# Revit family: PlumFix_Tap_ABEY_Stile_Wall Mixer & Basin Spout Set
name_source: partatom
category: Plumbing Fixtures
revit_build: Autodesk Revit 2015 (Build: 20140223_1515(x64)
units: mm (PartAtom-declared; Revit-internal decimal feet)

## types (5) — shared parameters
CW Connection = Yes
Description = Stile Wall Mixer & Basin Spout Set
HW Connection = Yes
Manufacturer = Abey Australia
Manufacturer_Overall Depth = 201 mm
Manufacturer_Overall Height = 110 mm
Manufacturer_Overall Width = 250 mm  [stored 0.82021 ft]
Manufacturer_URL__Product Specific = https://www.abey.com.au
URL = https://www.abey.com.au
Vent Connection = No
Waste Connection = No
zero-valued in all types: CWFU, Cost, HWFU, WFU

## per-type parameters (varying)
| type | Manufacturer_Spec Code | Model | PlumbingMaterial_ANZRS | Type Comments |
| Chrome | 700197+300033 | 700197+300033 | z_Abey_Chrome | Chrome Finish |
| Black | 700197B+300033B | 700197B+300033B | z_Abey_Black | Black Finish |
| Brushed Nickel | 700197BN+300033BN | 700197BN+300033BN | z_Abey_Brushed Nickel | Brushed Nickel Finish |
| Graphite | 700197GR+300033GR | 700197GR+300033GR | z_Abey_Graphite | Graphite Finish |
| Rose Gold | 700197RG+300033RG | 700197RG+300033RG | z_Abey_Rose Gold | Rose Gold Finish |

note: [stored X ft] marks values corroborated as IEEE doubles in the binary element streams (Revit-internal decimal feet)

## geometry (parser evidence)
native form markers: Sweep x2
no freeform markers — native parametric forms only
